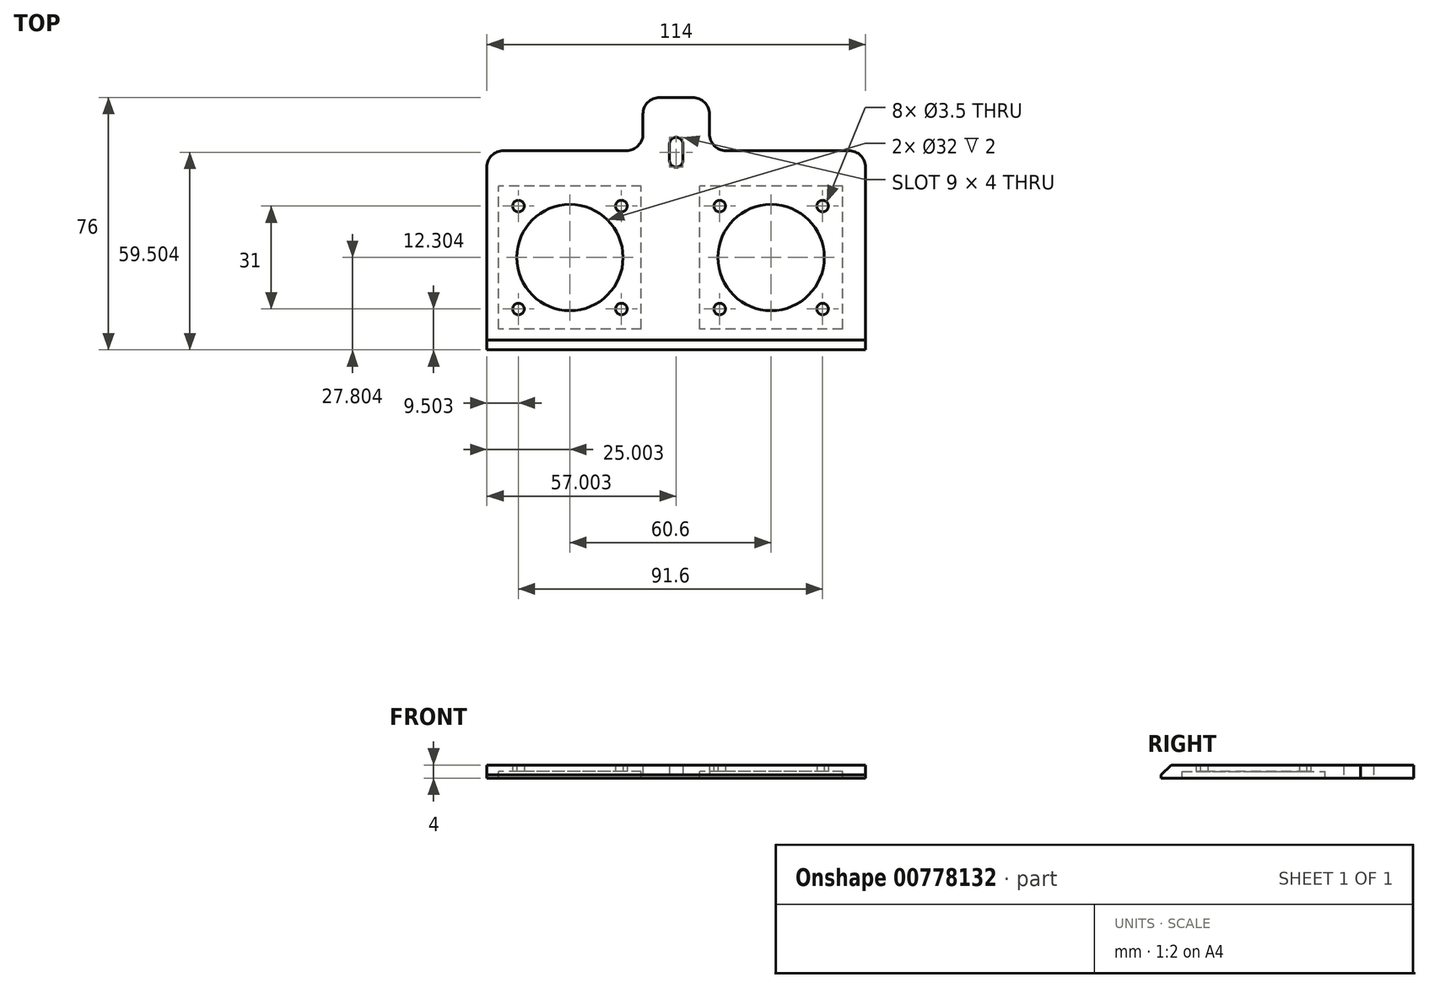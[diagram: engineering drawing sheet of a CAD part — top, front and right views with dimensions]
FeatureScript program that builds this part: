
annotation { "Feature Type Name" : "Feature", "Feature Type Description" : "" }
export const myFeature = defineFeature(function(context is Context, id is Id, definition is map)
    precondition{}
    {
        {
            var Q0;
            Q0=qCreatedBy(makeId("Top.planeOp"),FACE);
            var sketch = newSketch(context, id + "F0", { "sketchPlane" : qUnion([Q0])});
            skLineSegment(sketch, "E0", {"start": v(-55.62, 27.94) * mm, "end": v(-55.62, -32.06) * mm});
            skLineSegment(sketch, "E1", {"start": v(-55.62, -32.06) * mm, "end": v(58.38, -32.06) * mm});
            skLineSegment(sketch, "E2", {"start": v(58.38, -32.06) * mm, "end": v(58.38, 27.94) * mm});
            skLineSegment(sketch, "E3", {"start": v(58.38, 27.94) * mm, "end": v(11.38, 27.94) * mm});
            skLineSegment(sketch, "E4", {"start": v(11.38, 27.94) * mm, "end": v(11.38, 43.94) * mm});
            skLineSegment(sketch, "E5", {"start": v(11.38, 43.94) * mm, "end": v(-8.62, 43.94) * mm});
            skLineSegment(sketch, "E6", {"start": v(-8.62, 43.94) * mm, "end": v(-8.62, 27.94) * mm});
            skLineSegment(sketch, "E7", {"start": v(-8.62, 27.94) * mm, "end": v(-55.62, 27.94) * mm});
            skLineSegment(sketch, "E8.bottom", {"start": v(-15.12, -19.76) * mm, "end": v(-46.12, -19.76) * mm, "construction": true});
            skLineSegment(sketch, "E8.top", {"start": v(-15.12, 11.24) * mm, "end": v(-46.12, 11.24) * mm, "construction": true});
            skLineSegment(sketch, "E8.left", {"start": v(-15.12, -19.76) * mm, "end": v(-15.12, 11.24) * mm, "construction": true});
            skLineSegment(sketch, "E8.right", {"start": v(-46.12, -19.76) * mm, "end": v(-46.12, 11.24) * mm, "construction": true});
            skPoint(sketch, "E8.middle", {"position": v(-30.62, -4.26) * mm});
            skLineSegment(sketch, "E9.bottom", {"start": v(45.48, -19.76) * mm, "end": v(14.48, -19.76) * mm, "construction": true});
            skLineSegment(sketch, "E9.top", {"start": v(45.48, 11.24) * mm, "end": v(14.48, 11.24) * mm, "construction": true});
            skLineSegment(sketch, "E9.left", {"start": v(45.48, -19.76) * mm, "end": v(45.48, 11.24) * mm, "construction": true});
            skLineSegment(sketch, "E9.right", {"start": v(14.48, -19.76) * mm, "end": v(14.48, 11.24) * mm, "construction": true});
            skPoint(sketch, "E9.middle", {"position": v(29.98, -4.26) * mm});
            skLineSegment(sketch, "E10", {"start": v(-55.62, 22.11) * mm, "end": v(-46.12, 22.11) * mm, "construction": true});
            skLineSegment(sketch, "E11", {"start": v(-82.7, 27.94) * mm, "end": v(-82.7, 11.24) * mm, "construction": true});
            skLineSegment(sketch, "E12", {"start": v(-71.32, 27.94) * mm, "end": v(-71.32, -4.26) * mm, "construction": true});
            skLineSegment(sketch, "E13", {"start": v(58.38, 22.92) * mm, "end": v(45.48, 22.92) * mm, "construction": true});
            skCircle(sketch, "E14", {"center": v(-46.12, 11.24) * mm, "radius": 1.75 * mm});
            skCircle(sketch, "E15", {"center": v(-15.12, 11.24) * mm, "radius": 1.75 * mm});
            skCircle(sketch, "E16", {"center": v(-15.12, -19.76) * mm, "radius": 1.75 * mm});
            skCircle(sketch, "E17", {"center": v(-46.12, -19.76) * mm, "radius": 1.75 * mm});
            skCircle(sketch, "E18", {"center": v(14.48, 11.24) * mm, "radius": 1.75 * mm});
            skCircle(sketch, "E19", {"center": v(14.48, -19.76) * mm, "radius": 1.75 * mm});
            skCircle(sketch, "E20", {"center": v(45.48, -19.76) * mm, "radius": 1.75 * mm});
            skCircle(sketch, "E21", {"center": v(45.48, 11.24) * mm, "radius": 1.75 * mm});
            skCircle(sketch, "E22", {"center": v(-30.62, -4.26) * mm, "radius": 16 * mm});
            skCircle(sketch, "E23", {"center": v(29.98, -4.26) * mm, "radius": 16 * mm});
            skLineSegment(sketch, "E24", {"start": v(-14.49, 43.94) * mm, "end": v(-14.49, 29.94) * mm, "construction": true});
            skLineSegment(sketch, "E25", {"start": v(-14.49, 29.94) * mm, "end": v(-14.49, 24.94) * mm, "construction": true});
            skLineSegment(sketch, "E26", {"start": v(-8.62, 52.3) * mm, "end": v(1.38, 52.3) * mm, "construction": true});
            skCircle(sketch, "E27", {"center": v(1.38, 29.94) * mm, "radius": 2 * mm});
            skCircle(sketch, "E28", {"center": v(1.38, 24.94) * mm, "radius": 2 * mm});
            skLineSegment(sketch, "E29", {"start": v(-0.62, 29.94) * mm, "end": v(-0.62, 24.94) * mm});
            skLineSegment(sketch, "E30", {"start": v(3.38, 24.94) * mm, "end": v(3.38, 29.94) * mm});
            skLineSegment(sketch, "E31.bottom", {"start": v(51.48, -25.76) * mm, "end": v(8.48, -25.76) * mm});
            skLineSegment(sketch, "E31.top", {"start": v(51.48, 17.24) * mm, "end": v(8.48, 17.24) * mm});
            skLineSegment(sketch, "E31.left", {"start": v(51.48, -25.76) * mm, "end": v(51.48, 17.24) * mm});
            skLineSegment(sketch, "E31.right", {"start": v(8.48, -25.76) * mm, "end": v(8.48, 17.24) * mm});
            skLineSegment(sketch, "E32.bottom", {"start": v(-9.12, -25.76) * mm, "end": v(-52.12, -25.76) * mm});
            skLineSegment(sketch, "E32.top", {"start": v(-9.12, 17.24) * mm, "end": v(-52.12, 17.24) * mm});
            skLineSegment(sketch, "E32.left", {"start": v(-9.12, -25.76) * mm, "end": v(-9.12, 17.24) * mm});
            skLineSegment(sketch, "E32.right", {"start": v(-52.12, -25.76) * mm, "end": v(-52.12, 17.24) * mm});
            skSolve(sketch);
        }
        {
            var Q0;
            Q0=makeQuery(id+"F0.imprint","IMPRINT",FACE,{"disambiguationData":[TD([[makeQuery(id+"F0.imprint","IMPRINT",EDGE,{"derivedFrom":sQuery(id+"F0.wireOp",EDGE,"E0")}),1.0]])]});
            var Q1;
            Q1=makeQuery(id+"F0.imprint","IMPRINT",FACE,{"disambiguationData":[TD([[makeQuery(id+"F0.imprint","IMPRINT",EDGE,{"derivedFrom":sQuery(id+"F0.wireOp",EDGE,"E14")}),-1.0]])]});
            var Q2;
            Q2=makeQuery(id+"F0.imprint","IMPRINT",FACE,{"disambiguationData":[TD([[makeQuery(id+"F0.imprint","IMPRINT",EDGE,{"derivedFrom":sQuery(id+"F0.wireOp",EDGE,"E18")}),-1.0]])]});
            extrude(context, id + "F1", {"entities" : qUnion([Q0, Q1, Q2]), "depth" : 4 * mm, "offsetDistance" : 25 * mm});
        }
        {
            var Q0;
            Q0=makeQuery(id+"F1.opExtrude","SWEPT_EDGE",EDGE,{"disambiguationData":[OSD([sQuery(id+"F0.wireOp",EDGE,"E5"),sQuery(id+"F0.wireOp",EDGE,"E6")])]});
            var Q1;
            Q1=makeQuery(id+"F1.opExtrude","SWEPT_EDGE",EDGE,{"disambiguationData":[OSD([sQuery(id+"F0.wireOp",EDGE,"E6"),sQuery(id+"F0.wireOp",EDGE,"E7")])]});
            var Q2;
            Q2=makeQuery(id+"F1.opExtrude","SWEPT_EDGE",EDGE,{"disambiguationData":[OSD([sQuery(id+"F0.wireOp",EDGE,"E0"),sQuery(id+"F0.wireOp",EDGE,"E7")])]});
            var Q3;
            Q3=makeQuery(id+"F1.opExtrude","SWEPT_EDGE",EDGE,{"disambiguationData":[OSD([sQuery(id+"F0.wireOp",EDGE,"E4"),sQuery(id+"F0.wireOp",EDGE,"E5")])]});
            var Q4;
            Q4=makeQuery(id+"F1.opExtrude","SWEPT_EDGE",EDGE,{"disambiguationData":[OSD([sQuery(id+"F0.wireOp",EDGE,"E3"),sQuery(id+"F0.wireOp",EDGE,"E4")])]});
            var Q5;
            Q5=makeQuery(id+"F1.opExtrude","SWEPT_EDGE",EDGE,{"disambiguationData":[OSD([sQuery(id+"F0.wireOp",EDGE,"E2"),sQuery(id+"F0.wireOp",EDGE,"E3")])]});
            fillet(context, id + "F2", {"entities" : qUnion([Q0, Q1, Q2, Q3, Q4, Q5]), "radius" : 5 * mm, "tangentPropagation" : true, "allowEdgeOverflow" : false});
        }
        {
            var Q0;
            Q0=makeQuery(id+"F1.opExtrude","CAP_EDGE",EDGE,{"disambiguationData":[OSD([sQuery(id+"F0.wireOp",EDGE,"E1")])],"isStart":false});
            chamfer(context, id + "F3", {"entities" : qUnion([Q0]), "width" : 3 * mm, "tangentPropagation" : true});
        }
        {
            var Q0;
            Q0=makeQuery(id+"F0.imprint","IMPRINT",FACE,{"disambiguationData":[TD([[makeQuery(id+"F0.imprint","IMPRINT",EDGE,{"derivedFrom":sQuery(id+"F0.wireOp",EDGE,"E14")}),-1.0]])]});
            var Q1;
            Q1=makeQuery(id+"F0.imprint","IMPRINT",FACE,{"disambiguationData":[TD([[makeQuery(id+"F0.imprint","IMPRINT",EDGE,{"derivedFrom":sQuery(id+"F0.wireOp",EDGE,"E18")}),-1.0]])]});
            extrude(context, id + "F4", {"entities" : qUnion([Q0, Q1]), "operationType" : NewBodyOperationType.REMOVE, "oppositeDirection" : true, "depth" : 4 * mm, "offsetDistance" : 25 * mm, "hasSecondDirection" : true, "secondDirectionOppositeDirection" : false, "secondDirectionDepth" : 2 * mm});
        }
    });
